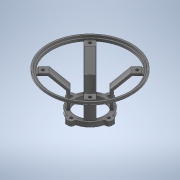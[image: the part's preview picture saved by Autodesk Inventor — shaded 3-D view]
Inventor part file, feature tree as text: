
AUTODESK INVENTOR PART (.ipt)
format: ipt  version: 2020 (Build 240168000, 168)  size: 469,504 bytes
history: native  units: mm
features: other x11, sketch x8, revolve x4, extrude x3, projected_geometry x3, pattern_circular x1, fillet x1
ambient origin geometry x8: Origin, YZ Plane, XZ Plane, XY Plane, X Axis, Y Axis, Z Axis, Center Point
bodies: Body1 (feature_tree)
feature tree (31):
  other  "Твердое тело1"
  extrude  "Выдавливание1"  Depth=34.0mm
  other  "РабПлоскость1"
  other  "РабОсь1"
  revolve  "Вращение1"
  sketch  "Эскиз3"
  other  "РабТочка1"
  extrude  "Выдавливание2"  Depth=45.0mm
  other  "РабТочка2"
  other  "РабТочка3"
  other  "РабТочка4"
  other  "РабПлоскость2"
  sketch  "Эскиз5"
  revolve  "Вращение2"
  revolve  "Вращение3"
  pattern_circular  "Круговой массив1"  Angle=45.0deg  [1 undecoded]
  extrude  "Выдавливание3"  Depth=3.3mm
  revolve  "Вращение4"
  sketch  "Эскиз8"
  fillet  "Сопряжение1"  Radius=9.0mm
  sketch  "Эскиз1"
  sketch  "Эскиз2"
  sketch  "Эскиз4"
  projected_geometry  "Спроецированная петля1"
  projected_geometry  "Спроецированная петля2"
  projected_geometry  "Спроецированная петля3"
  other  "РабПлоскость3"
  other  "РабПлоскость4"
  other  "РабПлоскость5"
  sketch  "Эскиз6"
  sketch  "Эскиз7"
note: 1 required parameter value undecoded (feature->parameter linkage not recoverable at this tier; creation-order binding heuristic only, values carry confidence <= 0.55)
